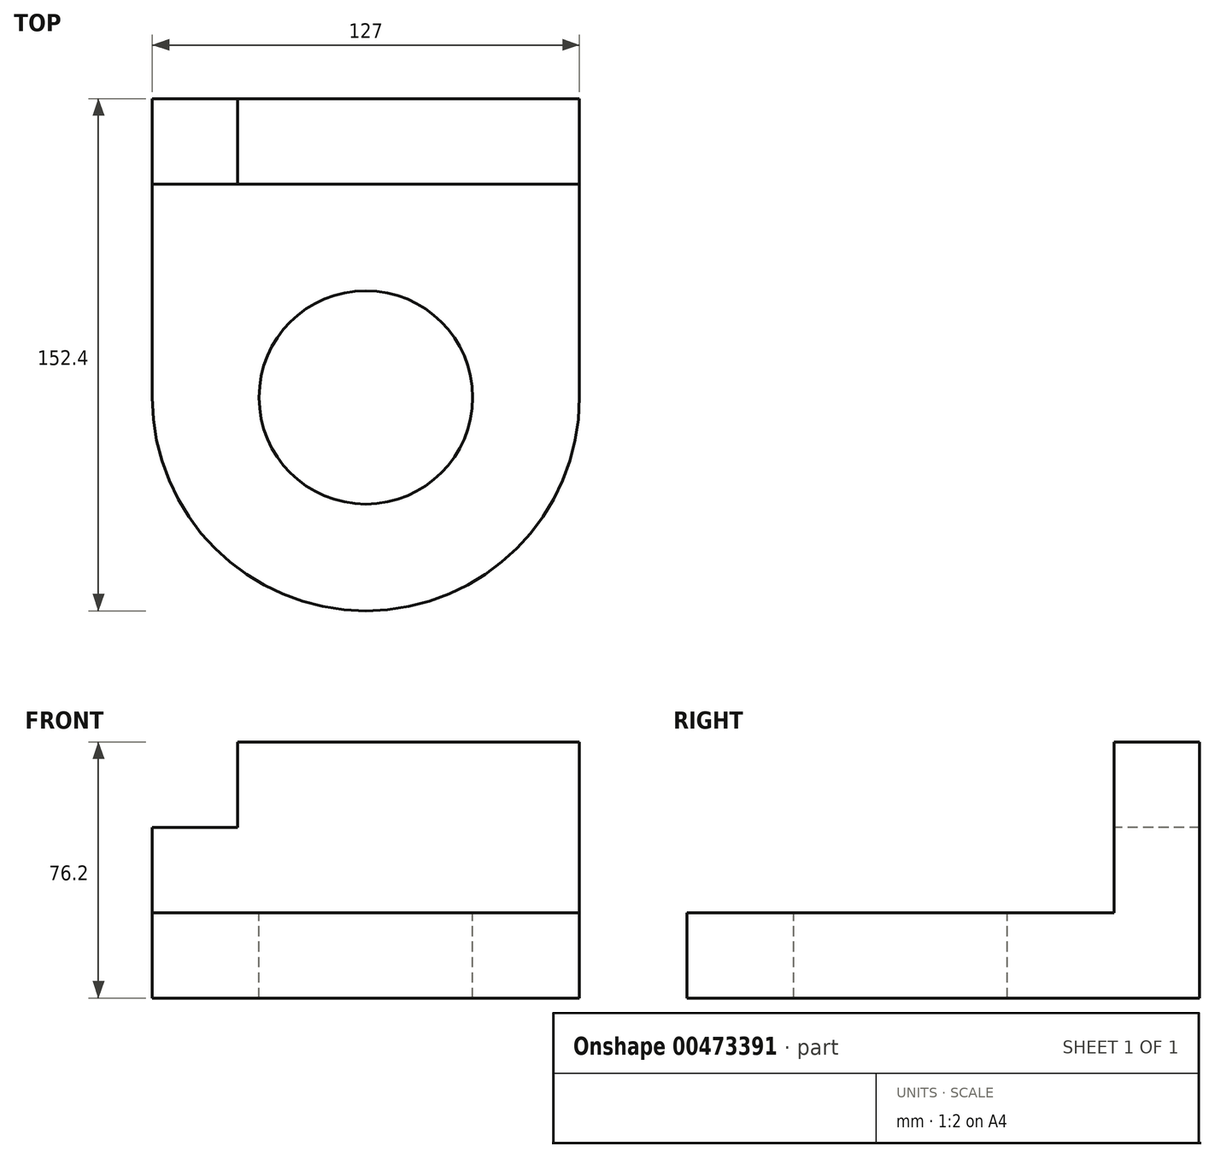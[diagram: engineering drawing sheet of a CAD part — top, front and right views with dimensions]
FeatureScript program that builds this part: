
annotation { "Feature Type Name" : "Feature", "Feature Type Description" : "" }
export const myFeature = defineFeature(function(context is Context, id is Id, definition is map)
    precondition{}
    {
        {
            var Q0;
            Q0=qCreatedBy(makeId("Front.planeOp"),FACE);
            var sketch = newSketch(context, id + "F0", { "sketchPlane" : qUnion([Q0])});
            skLineSegment(sketch, "E0.bottom", {"start": v(63.5, 38.1) * mm, "end": v(-63.5, 38.1) * mm});
            skLineSegment(sketch, "E0.top", {"start": v(63.5, -38.1) * mm, "end": v(-63.5, -38.1) * mm});
            skLineSegment(sketch, "E0.left", {"start": v(63.5, 38.1) * mm, "end": v(63.5, -38.1) * mm});
            skLineSegment(sketch, "E0.right", {"start": v(-63.5, 38.1) * mm, "end": v(-63.5, -38.1) * mm});
            skPoint(sketch, "E0.middle", {"position": v(0, 0) * mm});
            skSolve(sketch);
        }
        {
            var Q0;
            Q0=makeQuery(id+"F0.imprint","IMPRINT",FACE,{"disambiguationData":[TD([[makeQuery(id+"F0.imprint","IMPRINT",EDGE,{"derivedFrom":sQuery(id+"F0.wireOp",EDGE,"E0.bottom")}),1.0]])]});
            extrude(context, id + "F1", {"entities" : qUnion([Q0]), "oppositeDirection" : true, "depth" : 25.4 * mm});
        }
        {
            var Q0;
            Q0=makeQuery(id+"F1.opExtrude","CAP_FACE",FACE,{"disambiguationData":[OSD([sQuery(id+"F0.wireOp",EDGE,"E0.bottom"),sQuery(id+"F0.wireOp",EDGE,"E0.top"),sQuery(id+"F0.wireOp",EDGE,"E0.left"),sQuery(id+"F0.wireOp",EDGE,"E0.right")])],"isStart":true});
            var sketch = newSketch(context, id + "F2", { "sketchPlane" : qUnion([Q0])});
            skLineSegment(sketch, "E1.bottom", {"start": v(-63.5, -38.1) * mm, "end": v(63.5, -38.1) * mm});
            skLineSegment(sketch, "E1.top", {"start": v(-63.5, -12.7) * mm, "end": v(63.5, -12.7) * mm});
            skLineSegment(sketch, "E1.left", {"start": v(-63.5, -38.1) * mm, "end": v(-63.5, -12.7) * mm});
            skLineSegment(sketch, "E1.right", {"start": v(63.5, -38.1) * mm, "end": v(63.5, -12.7) * mm});
            skSolve(sketch);
        }
        {
            var Q0;
            Q0=makeQuery(id+"F2.imprint","IMPRINT",FACE,{"disambiguationData":[TD([[makeQuery(id+"F2.imprint","IMPRINT",EDGE,{"derivedFrom":sQuery(id+"F2.wireOp",EDGE,"E1.bottom")}),-1.0]])]});
            extrude(context, id + "F3", {"entities" : qUnion([Q0]), "operationType" : NewBodyOperationType.ADD, "depth" : 127 * mm});
        }
        {
            var Q0;
            Q0=makeQuery(id+"F3.opExtrude","SWEPT_FACE",FACE,{"disambiguationData":[OSD([sQuery(id+"F2.wireOp",EDGE,"E1.top")])]});
            var sketch = newSketch(context, id + "F4", { "sketchPlane" : qUnion([Q0])});
            skLineSegment(sketch, "E2", {"start": v(0, -127) * mm, "end": v(0, 0) * mm});
            skLineSegment(sketch, "E3", {"start": v(-63.5, -63.5) * mm, "end": v(63.5, -63.5) * mm});
            skCircle(sketch, "E4", {"center": v(0, -63.5) * mm, "radius": 63.5 * mm});
            skSolve(sketch);
        }
        {
            var Q0;
            {var subQ0=sQuery(id+"F4.wireOp",EDGE,"E4");var subQ1=sQuery(id+"F2.wireOp",EDGE,"E1.top");var subQ2=makeQuery(id+"F3.opExtrude","CAP_EDGE",EDGE,{"disambiguationData":[OSD([subQ1])],"isStart":false});var subQ3=makeQuery(id+"F4.imprint","INTERSECT",VERTEX,{"derivedFrom":[subQ2,sQuery(id+"F4.wireOp",EDGE,"E2"),subQ0]});Q0=makeQuery(id+"F4.imprint","IMPRINT",FACE,{"disambiguationData":[TD([[makeQuery(id+"F4.imprint","IMPRINT",EDGE,{"disambiguationData":[TD([[subQ3,-1.0]])],"derivedFrom":subQ2}),1.0]])]});}
            var Q1;
            {var subQ0=sQuery(id+"F4.wireOp",EDGE,"E4");var subQ1=sQuery(id+"F2.wireOp",EDGE,"E1.top");var subQ2=makeQuery(id+"F3.opExtrude","CAP_EDGE",EDGE,{"disambiguationData":[OSD([subQ1])],"isStart":false});var subQ3=makeQuery(id+"F4.imprint","INTERSECT",VERTEX,{"derivedFrom":[subQ2,sQuery(id+"F4.wireOp",EDGE,"E2"),subQ0]});Q1=makeQuery(id+"F4.imprint","IMPRINT",FACE,{"disambiguationData":[TD([[makeQuery(id+"F4.imprint","IMPRINT",EDGE,{"disambiguationData":[TD([[subQ3,1.0]])],"derivedFrom":subQ2}),1.0]])]});}
            extrude(context, id + "F5", {"entities" : qUnion([Q0, Q1]), "operationType" : NewBodyOperationType.REMOVE, "oppositeDirection" : true, "depth" : 25.4 * mm});
        }
        {
            var Q0;
            Q0=makeQuery(id+"F3.opExtrude","SWEPT_FACE",FACE,{"disambiguationData":[OSD([sQuery(id+"F2.wireOp",EDGE,"E1.top")])]});
            var sketch = newSketch(context, id + "F6", { "sketchPlane" : qUnion([Q0])});
            skCircle(sketch, "E5", {"center": v(0, -63.5) * mm, "radius": 31.75 * mm});
            skSolve(sketch);
        }
        {
            var Q0;
            Q0=makeQuery(id+"F6.imprint","IMPRINT",FACE,{"disambiguationData":[TD([[makeQuery(id+"F6.imprint","IMPRINT",EDGE,{"derivedFrom":sQuery(id+"F6.wireOp",EDGE,"E5")}),1.0]])]});
            extrude(context, id + "F7", {"entities" : qUnion([Q0]), "operationType" : NewBodyOperationType.REMOVE, "endBound" : BoundingType.THROUGH_ALL, "oppositeDirection" : true, "depth" : 25.4 * mm});
        }
        {
            var Q0;
            Q0=makeQuery(id+"F1.opExtrude","CAP_FACE",FACE,{"disambiguationData":[OSD([sQuery(id+"F0.wireOp",EDGE,"E0.bottom"),sQuery(id+"F0.wireOp",EDGE,"E0.top"),sQuery(id+"F0.wireOp",EDGE,"E0.left"),sQuery(id+"F0.wireOp",EDGE,"E0.right")])],"isStart":true});
            var sketch = newSketch(context, id + "F8", { "sketchPlane" : qUnion([Q0])});
            skLineSegment(sketch, "E6.bottom", {"start": v(-63.5, 38.1) * mm, "end": v(-38.1, 38.1) * mm});
            skLineSegment(sketch, "E6.top", {"start": v(-63.5, 12.7) * mm, "end": v(-38.1, 12.7) * mm});
            skLineSegment(sketch, "E6.left", {"start": v(-63.5, 38.1) * mm, "end": v(-63.5, 12.7) * mm});
            skLineSegment(sketch, "E6.right", {"start": v(-38.1, 38.1) * mm, "end": v(-38.1, 12.7) * mm});
            skSolve(sketch);
        }
        {
            var Q0;
            Q0=makeQuery(id+"F8.imprint","IMPRINT",FACE,{"disambiguationData":[TD([[makeQuery(id+"F8.imprint","IMPRINT",EDGE,{"derivedFrom":sQuery(id+"F8.wireOp",EDGE,"E6.bottom")}),1.0]])]});
            extrude(context, id + "F9", {"entities" : qUnion([Q0]), "operationType" : NewBodyOperationType.REMOVE, "endBound" : BoundingType.THROUGH_ALL, "oppositeDirection" : true, "depth" : 25.4 * mm});
        }
    });
